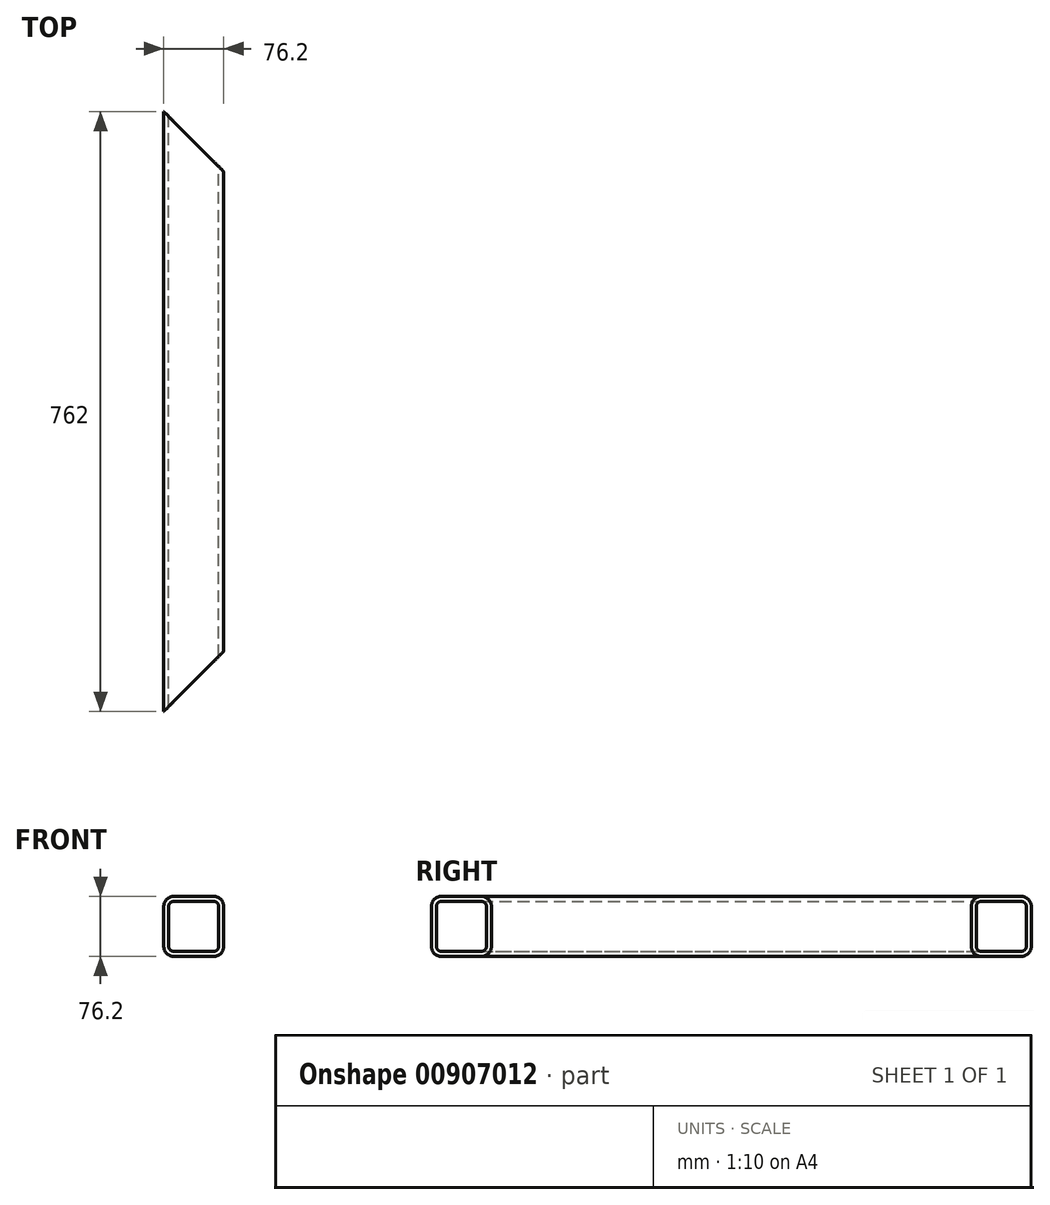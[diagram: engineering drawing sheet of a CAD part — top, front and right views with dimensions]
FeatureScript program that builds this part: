
annotation { "Feature Type Name" : "Feature", "Feature Type Description" : "" }
export const myFeature = defineFeature(function(context is Context, id is Id, definition is map)
    precondition{}
    {
        {
            var Q0;
            Q0=qCreatedBy(makeId("Front.planeOp"),FACE);
            var sketch = newSketch(context, id + "F0", { "sketchPlane" : qUnion([Q0])});
            skLineSegment(sketch, "E0.bottom", {"start": v(25.4, 38.1) * mm, "end": v(-25.4, 38.1) * mm});
            skLineSegment(sketch, "E0.top", {"start": v(25.4, -38.1) * mm, "end": v(-25.4, -38.1) * mm});
            skLineSegment(sketch, "E0.left", {"start": v(38.1, 25.4) * mm, "end": v(38.1, -25.4) * mm});
            skLineSegment(sketch, "E0.right", {"start": v(-38.1, 25.4) * mm, "end": v(-38.1, -25.4) * mm});
            skPoint(sketch, "E0.middle", {"position": v(0, 0) * mm});
            skPoint(sketch, "E1.visualSharp", {"position": v(-38.1, 38.1) * mm});
            skArc(sketch, "E1.filletArc", {"start": v(-25.4, 38.1) * mm, "mid": v(-34.38, 34.38) * mm, "end": v(-38.1, 25.4) * mm});
            skPoint(sketch, "E2.visualSharp", {"position": v(38.1, 38.1) * mm});
            skArc(sketch, "E2.filletArc", {"start": v(38.1, 25.4) * mm, "mid": v(34.38, 34.38) * mm, "end": v(25.4, 38.1) * mm});
            skPoint(sketch, "E3.visualSharp", {"position": v(38.1, -38.1) * mm});
            skArc(sketch, "E3.filletArc", {"start": v(25.4, -38.1) * mm, "mid": v(34.38, -34.38) * mm, "end": v(38.1, -25.4) * mm});
            skPoint(sketch, "E4.visualSharp", {"position": v(-38.1, -38.1) * mm});
            skArc(sketch, "E4.filletArc", {"start": v(-38.1, -25.4) * mm, "mid": v(-34.38, -34.38) * mm, "end": v(-25.4, -38.1) * mm});
            skArc(sketch, "E5.0", {"start": v(31.75, 25.4) * mm, "mid": v(29.9, 29.9) * mm, "end": v(25.4, 31.75) * mm});
            skLineSegment(sketch, "E5.1", {"start": v(31.75, 25.4) * mm, "end": v(31.75, -25.4) * mm});
            skLineSegment(sketch, "E5.2", {"start": v(25.4, 31.75) * mm, "end": v(-25.4, 31.75) * mm});
            skArc(sketch, "E5.3", {"start": v(25.4, -31.75) * mm, "mid": v(29.9, -29.9) * mm, "end": v(31.75, -25.4) * mm});
            skArc(sketch, "E5.4", {"start": v(-25.4, 31.75) * mm, "mid": v(-29.9, 29.9) * mm, "end": v(-31.75, 25.4) * mm});
            skLineSegment(sketch, "E5.5", {"start": v(-31.75, 25.4) * mm, "end": v(-31.75, -25.4) * mm});
            skArc(sketch, "E5.6", {"start": v(-31.75, -25.4) * mm, "mid": v(-29.9, -29.9) * mm, "end": v(-25.4, -31.75) * mm});
            skLineSegment(sketch, "E5.7", {"start": v(25.4, -31.75) * mm, "end": v(-25.4, -31.75) * mm});
            skSolve(sketch);
        }
        {
            var Q0;
            Q0=makeQuery(id+"F0.imprint","IMPRINT",FACE,{"disambiguationData":[TD([[makeQuery(id+"F0.imprint","IMPRINT",EDGE,{"derivedFrom":sQuery(id+"F0.wireOp",EDGE,"E0.bottom")}),1.0]])]});
            extrude(context, id + "F1", {"entities" : qUnion([Q0]), "depth" : 762 * mm, "offsetDistance" : 25.4 * mm, "symmetric" : true});
        }
        {
            var Q0;
            Q0=qCreatedBy(makeId("Top.planeOp"),FACE);
            var sketch = newSketch(context, id + "F2", { "sketchPlane" : qUnion([Q0])});
            skLineSegment(sketch, "E6.0", {"start": v(-38.1, -381) * mm, "end": v(-38.1, 381) * mm});
            skLineSegment(sketch, "E7.0", {"start": v(38.1, -381) * mm, "end": v(38.1, 381) * mm});
            skLineSegment(sketch, "E8", {"start": v(-38.1, 381) * mm, "end": v(38.1, 381) * mm});
            skLineSegment(sketch, "E9", {"start": v(38.1, 381) * mm, "end": v(38.1, 304.8) * mm});
            skLineSegment(sketch, "E10", {"start": v(38.1, 304.8) * mm, "end": v(-38.1, 381) * mm});
            skLineSegment(sketch, "E11", {"start": v(-38.1, -381) * mm, "end": v(38.1, -381) * mm});
            skLineSegment(sketch, "E12", {"start": v(38.1, -381) * mm, "end": v(38.1, -304.8) * mm});
            skLineSegment(sketch, "E13", {"start": v(38.1, -304.8) * mm, "end": v(-38.1, -381) * mm});
            skSolve(sketch);
        }
        {
            var Q0;
            {var subQ2=sQuery(id+"F2.wireOp",EDGE,"E11");Q0=makeQuery(id+"F2.imprint","IMPRINT",FACE,{"disambiguationData":[TD([[makeQuery(id+"F2.imprint","IMPRINT",EDGE,{"derivedFrom":subQ2}),1.0]])]});}
            var Q1;
            {var subQ0=sQuery(id+"F2.wireOp",EDGE,"E8");Q1=makeQuery(id+"F2.imprint","IMPRINT",FACE,{"disambiguationData":[TD([[makeQuery(id+"F2.imprint","IMPRINT",EDGE,{"derivedFrom":subQ0}),-1.0]])]});}
            extrude(context, id + "F3", {"entities" : qUnion([Q0, Q1]), "operationType" : NewBodyOperationType.REMOVE, "oppositeDirection" : true, "depth" : 101.6 * mm, "offsetDistance" : 25.4 * mm, "symmetric" : true});
        }
    });
